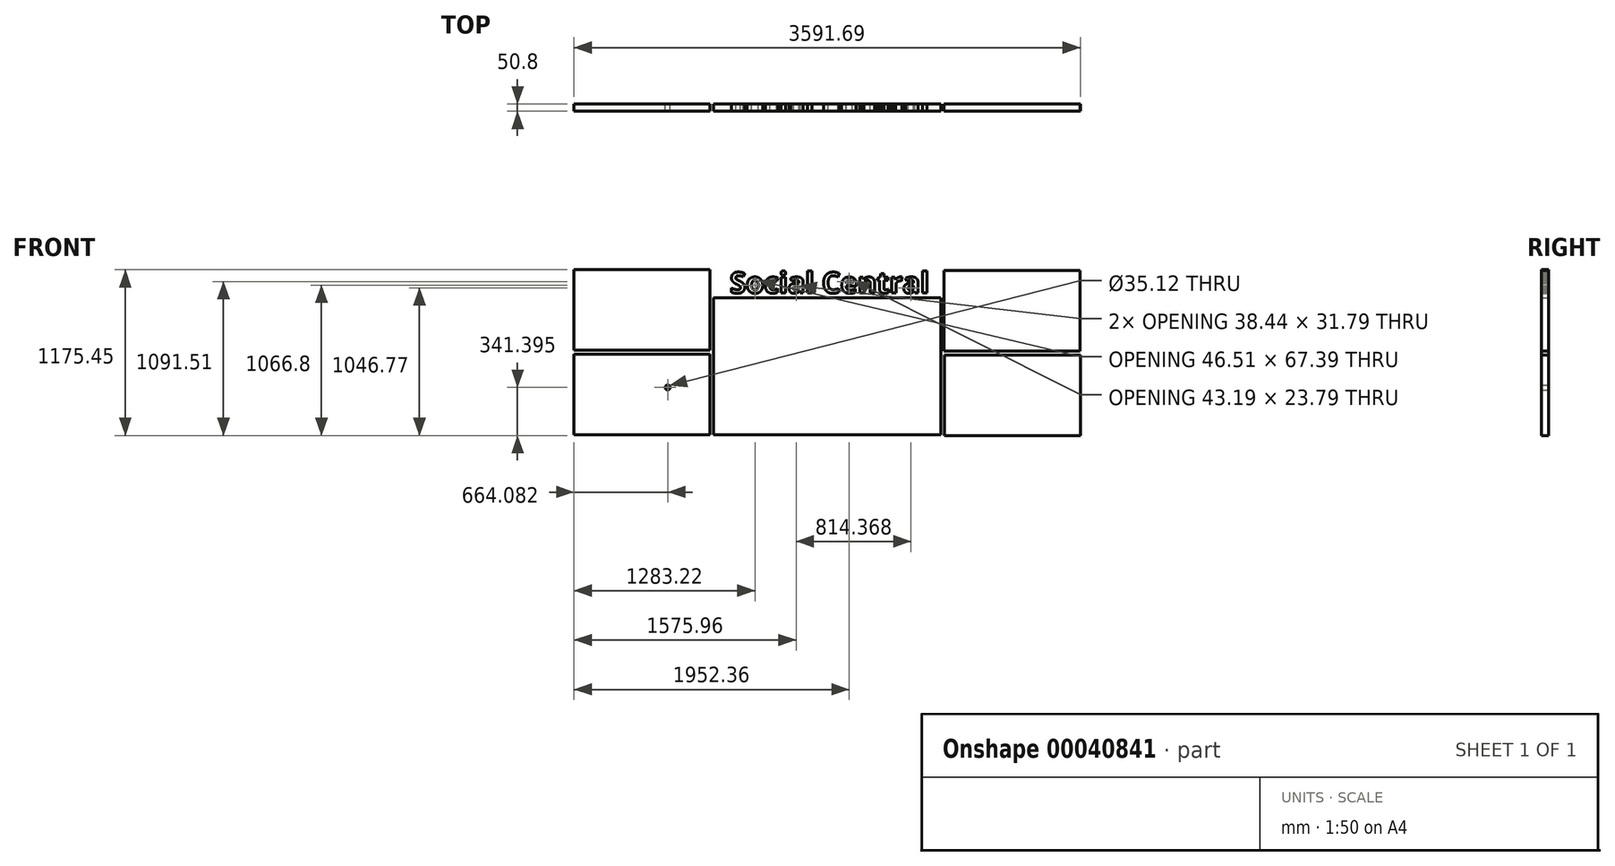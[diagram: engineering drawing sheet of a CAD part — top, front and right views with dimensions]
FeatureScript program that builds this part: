
annotation { "Feature Type Name" : "Feature", "Feature Type Description" : "" }
export const myFeature = defineFeature(function(context is Context, id is Id, definition is map)
    precondition{}
    {
        {
            var Q0;
            Q0=qCreatedBy(makeId("Front.planeOp"),FACE);
            var sketch = newSketch(context, id + "F0", { "sketchPlane" : qUnion([Q0])});
            skLineSegment(sketch, "E0.bottom", {"start": v(-823.82, 509.58) * mm, "end": v(789.08, 509.58) * mm});
            skLineSegment(sketch, "E0.top", {"start": v(-823.82, -461.97) * mm, "end": v(789.08, -461.97) * mm});
            skLineSegment(sketch, "E0.left", {"start": v(-823.82, 509.58) * mm, "end": v(-823.82, -461.97) * mm});
            skLineSegment(sketch, "E0.right", {"start": v(789.08, 509.58) * mm, "end": v(789.08, -461.97) * mm});
            skLineSegment(sketch, "E1.bottom", {"start": v(814.28, 703.8) * mm, "end": v(1779.48, 703.8) * mm});
            skLineSegment(sketch, "E1.top", {"start": v(814.28, 132.3) * mm, "end": v(1779.48, 132.3) * mm});
            skLineSegment(sketch, "E1.left", {"start": v(814.28, 703.8) * mm, "end": v(814.28, 132.3) * mm});
            skLineSegment(sketch, "E1.right", {"start": v(1779.48, 703.8) * mm, "end": v(1779.48, 132.3) * mm});
            skLineSegment(sketch, "E2.bottom", {"start": v(814.54, 104.7) * mm, "end": v(1779.74, 104.7) * mm});
            skLineSegment(sketch, "E2.top", {"start": v(814.54, -466.8) * mm, "end": v(1779.74, -466.8) * mm});
            skLineSegment(sketch, "E2.left", {"start": v(814.54, 104.7) * mm, "end": v(814.54, -466.8) * mm});
            skLineSegment(sketch, "E2.right", {"start": v(1779.74, 104.7) * mm, "end": v(1779.74, -466.8) * mm});
            skLineSegment(sketch, "E3", {"start": v(-1864.87, -1338.27) * mm, "end": v(1838.98, -1338.27) * mm});
            skLineSegment(sketch, "E4.top", {"start": v(-1811.7, -461.97) * mm, "end": v(-846.5, -461.97) * mm});
            skLineSegment(sketch, "E4.right", {"start": v(-846.5, 109.53) * mm, "end": v(-846.5, -461.97) * mm});
            skLineSegment(sketch, "E4.bottom", {"start": v(-1811.7, 109.53) * mm, "end": v(-846.5, 109.53) * mm});
            skLineSegment(sketch, "E5.right", {"start": v(-846.75, 708.64) * mm, "end": v(-846.75, 137.14) * mm});
            skLineSegment(sketch, "E5.top", {"start": v(-1811.95, 137.14) * mm, "end": v(-846.75, 137.14) * mm});
            skLineSegment(sketch, "E5.bottom", {"start": v(-1811.95, 708.64) * mm, "end": v(-846.75, 708.64) * mm});
            skLineSegment(sketch, "E4.left", {"start": v(-1811.7, 109.53) * mm, "end": v(-1811.7, -461.97) * mm});
            skLineSegment(sketch, "E5.left", {"start": v(-1811.95, 708.64) * mm, "end": v(-1811.95, 137.14) * mm});
            skLineSegment(sketch, "E6.bottom", {"start": v(-1689.25, -80.3) * mm, "end": v(-956.64, -80.3) * mm});
            skLineSegment(sketch, "E6.top", {"start": v(-1689.25, -266.55) * mm, "end": v(-956.64, -266.55) * mm});
            skLineSegment(sketch, "E6.left", {"start": v(-1689.25, -80.3) * mm, "end": v(-1689.25, -266.55) * mm});
            skLineSegment(sketch, "E6.right", {"start": v(-956.64, -80.3) * mm, "end": v(-956.64, -266.55) * mm});
            skCircle(sketch, "E7", {"center": v(-1147.87, -125.42) * mm, "radius": 17.56 * mm});
            skSolve(sketch);
        }
        {
            var Q0;
            Q0=qCreatedBy(makeId("Front.planeOp"),FACE);
            var sketch = newSketch(context, id + "F1", { "sketchPlane" : qUnion([Q0])});
            skText(sketch, "E8", { "text": "Social Central", "fontName": "OpenSans-Bold.ttf"});
            const initialGuessF1  = {"E8": [-0.7064, 0.5436, 1, 0, 0.14873]};
            skSetInitialGuess(sketch, initialGuessF1);
            skSolve(sketch);
        }
        {
            var Q0;
            Q0=makeQuery(id+"F0.imprint","IMPRINT",FACE,{"disambiguationData":[TD([[makeQuery(id+"F0.imprint","IMPRINT",EDGE,{"derivedFrom":sQuery(id+"F0.wireOp",EDGE,"E5.right")}),-1.0]])]});
            var Q1;
            Q1=makeQuery(id+"F0.imprint","IMPRINT",FACE,{"disambiguationData":[TD([[makeQuery(id+"F0.imprint","IMPRINT",EDGE,{"derivedFrom":sQuery(id+"F0.wireOp",EDGE,"E4.top")}),1.0]])]});
            var Q2;
            Q2=makeQuery(id+"F0.imprint","IMPRINT",FACE,{"disambiguationData":[TD([[makeQuery(id+"F0.imprint","IMPRINT",EDGE,{"derivedFrom":sQuery(id+"F0.wireOp",EDGE,"E0.bottom")}),-1.0]])]});
            var Q3;
            Q3=makeQuery(id+"F0.imprint","IMPRINT",FACE,{"disambiguationData":[TD([[makeQuery(id+"F0.imprint","IMPRINT",EDGE,{"derivedFrom":sQuery(id+"F0.wireOp",EDGE,"E6.bottom")}),-1.0]])]});
            var Q4;
            Q4=makeQuery(id+"F0.imprint","IMPRINT",FACE,{"disambiguationData":[TD([[makeQuery(id+"F0.imprint","IMPRINT",EDGE,{"derivedFrom":sQuery(id+"F0.wireOp",EDGE,"E1.bottom")}),-1.0]])]});
            var Q5;
            Q5=makeQuery(id+"F0.imprint","IMPRINT",FACE,{"disambiguationData":[TD([[makeQuery(id+"F0.imprint","IMPRINT",EDGE,{"derivedFrom":sQuery(id+"F0.wireOp",EDGE,"E2.bottom")}),-1.0]])]});
            var Q6;
            Q6 = qSketchRegion(id + "F1", true);
            extrude(context, id + "F2", {"entities" : qUnion([Q0, Q1, Q2, Q3, Q4, Q5, Q6]), "depth" : 50.8 * mm});
        }
    });
